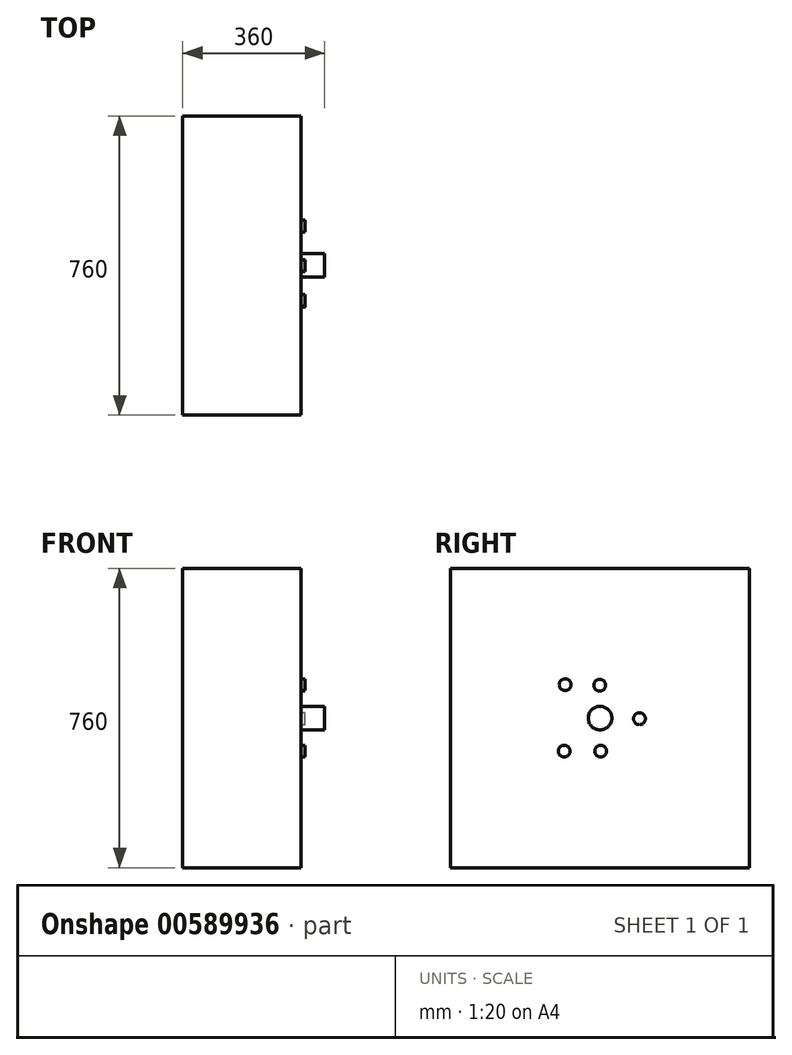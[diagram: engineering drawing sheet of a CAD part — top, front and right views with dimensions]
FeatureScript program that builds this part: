
annotation { "Feature Type Name" : "Feature", "Feature Type Description" : "" }
export const myFeature = defineFeature(function(context is Context, id is Id, definition is map)
    precondition{}
    {
        {
            var Q0;
            Q0=qCreatedBy(makeId("Right.planeOp"),FACE);
            var sketch = newSketch(context, id + "F0", { "sketchPlane" : qUnion([Q0])});
            skLineSegment(sketch, "E0.bottom", {"start": v(0, 0) * mm, "end": v(760, 0) * mm});
            skLineSegment(sketch, "E0.top", {"start": v(0, 760) * mm, "end": v(760, 760) * mm});
            skLineSegment(sketch, "E0.left", {"start": v(0, 0) * mm, "end": v(0, 760) * mm});
            skLineSegment(sketch, "E0.right", {"start": v(760, 0) * mm, "end": v(760, 760) * mm});
            skSolve(sketch);
        }
        {
            var Q0;
            Q0=makeQuery(id+"F0.imprint","IMPRINT",FACE,{"disambiguationData":[TD([[makeQuery(id+"F0.imprint","IMPRINT",EDGE,{"derivedFrom":sQuery(id+"F0.wireOp",EDGE,"E0.bottom")}),1.0]])]});
            extrude(context, id + "F1", {"entities" : qUnion([Q0]), "depth" : 300 * mm, "offsetDistance" : 25 * mm});
        }
        {
            var Q0;
            Q0=makeQuery(id+"F1.opExtrude","CAP_FACE",FACE,{"disambiguationData":[OSD([sQuery(id+"F0.wireOp",EDGE,"E0.bottom"),sQuery(id+"F0.wireOp",EDGE,"E0.top"),sQuery(id+"F0.wireOp",EDGE,"E0.left"),sQuery(id+"F0.wireOp",EDGE,"E0.right")])],"isStart":false});
            var sketch = newSketch(context, id + "F2", { "sketchPlane" : qUnion([Q0])});
            skCircle(sketch, "E1", {"center": v(380, 380) * mm, "radius": 30 * mm});
            skCircle(sketch, "E2", {"center": v(288.92, 296.12) * mm, "radius": 15 * mm});
            skCircle(sketch, "E3", {"center": v(291.3, 464.82) * mm, "radius": 15 * mm});
            skCircle(sketch, "E4", {"center": v(379.21, 463.63) * mm, "radius": 15 * mm});
            skCircle(sketch, "E5", {"center": v(480.2, 378.1) * mm, "radius": 15 * mm});
            skCircle(sketch, "E6", {"center": v(381.59, 296.12) * mm, "radius": 15 * mm});
            skSolve(sketch);
        }
        {
            var Q0;
            Q0=makeQuery(id+"F2.imprint","IMPRINT",FACE,{"disambiguationData":[TD([[makeQuery(id+"F2.imprint","IMPRINT",EDGE,{"derivedFrom":sQuery(id+"F2.wireOp",EDGE,"E1")}),1.0]])]});
            extrude(context, id + "F3", {"entities" : qUnion([Q0]), "depth" : 60 * mm, "offsetDistance" : 25 * mm});
        }
        {
            var Q0;
            Q0=makeQuery(id+"F2.imprint","IMPRINT",FACE,{"disambiguationData":[TD([[makeQuery(id+"F2.imprint","IMPRINT",EDGE,{"derivedFrom":sQuery(id+"F2.wireOp",EDGE,"E2")}),1.0]])]});
            var Q1;
            Q1=makeQuery(id+"F2.imprint","IMPRINT",FACE,{"disambiguationData":[TD([[makeQuery(id+"F2.imprint","IMPRINT",EDGE,{"derivedFrom":sQuery(id+"F2.wireOp",EDGE,"E3")}),1.0]])]});
            var Q2;
            Q2=makeQuery(id+"F2.imprint","IMPRINT",FACE,{"disambiguationData":[TD([[makeQuery(id+"F2.imprint","IMPRINT",EDGE,{"derivedFrom":sQuery(id+"F2.wireOp",EDGE,"E6")}),1.0]])]});
            var Q3;
            Q3=makeQuery(id+"F2.imprint","IMPRINT",FACE,{"disambiguationData":[TD([[makeQuery(id+"F2.imprint","IMPRINT",EDGE,{"derivedFrom":sQuery(id+"F2.wireOp",EDGE,"E4")}),1.0]])]});
            var Q4;
            Q4=makeQuery(id+"F2.imprint","IMPRINT",FACE,{"disambiguationData":[TD([[makeQuery(id+"F2.imprint","IMPRINT",EDGE,{"derivedFrom":sQuery(id+"F2.wireOp",EDGE,"E5")}),1.0]])]});
            extrude(context, id + "F4", {"entities" : qUnion([Q0, Q1, Q2, Q3, Q4]), "depth" : 10 * mm, "offsetDistance" : 25 * mm});
        }
    });
